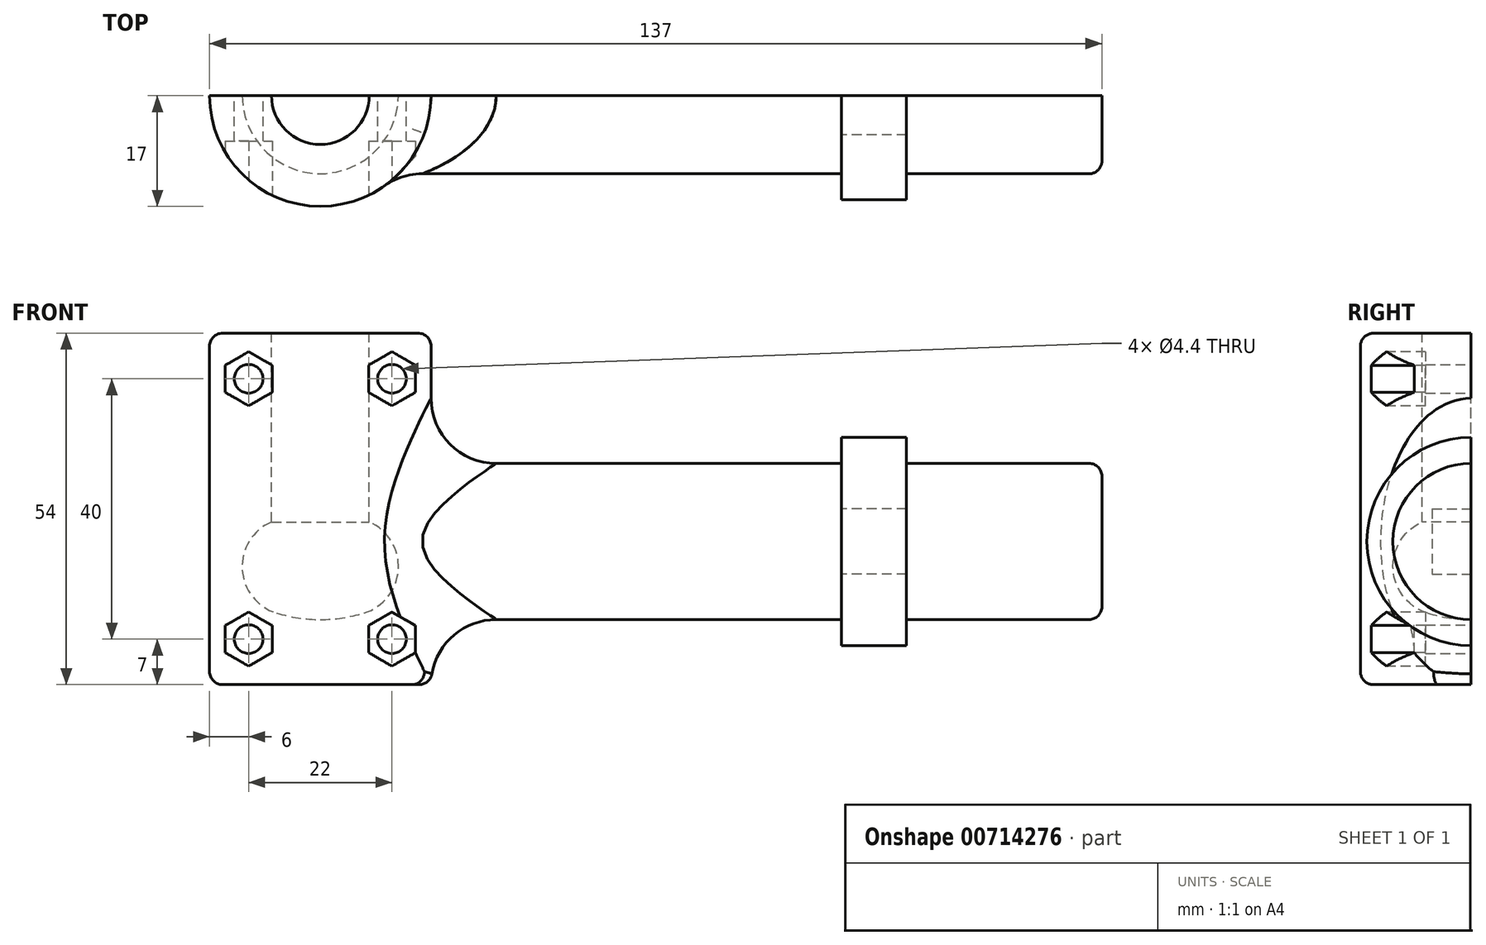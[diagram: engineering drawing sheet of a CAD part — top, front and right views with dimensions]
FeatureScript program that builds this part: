
annotation { "Feature Type Name" : "Feature", "Feature Type Description" : "" }
export const myFeature = defineFeature(function(context is Context, id is Id, definition is map)
    precondition{}
    {
        {
            var Q0;
            Q0=qCreatedBy(makeId("Front.planeOp"),FACE);
            var sketch = newSketch(context, id + "F0", { "sketchPlane" : qUnion([Q0])});
            skLineSegment(sketch, "E0", {"start": v(0, 0) * mm, "end": v(120, 0) * mm});
            skLineSegment(sketch, "E1", {"start": v(0, 0) * mm, "end": v(0, 12) * mm});
            skLineSegment(sketch, "E2", {"start": v(0, 12) * mm, "end": v(80, 12) * mm});
            skLineSegment(sketch, "E3", {"start": v(80, 12) * mm, "end": v(80, 16) * mm});
            skLineSegment(sketch, "E4", {"start": v(80, 16) * mm, "end": v(90, 16) * mm});
            skLineSegment(sketch, "E5", {"start": v(90, 16) * mm, "end": v(90, 12) * mm});
            skLineSegment(sketch, "E6", {"start": v(90, 12) * mm, "end": v(120, 12) * mm});
            skLineSegment(sketch, "E7", {"start": v(120, 12) * mm, "end": v(120, 0) * mm});
            skSolve(sketch);
        }
        {
            var Q0;
            Q0=makeQuery(id+"F0.imprint","IMPRINT",FACE,{"disambiguationData":[TD([[makeQuery(id+"F0.imprint","IMPRINT",EDGE,{"derivedFrom":sQuery(id+"F0.wireOp",EDGE,"E0")}),1.0]])]});
            var Q1;
            Q1=sQuery(id+"F0.wireOp",EDGE,"E0");
            revolve(context, id + "F1", {"surfaceOperationType" : NewSurfaceOperationType.NEW, "entities" : qUnion([Q0]), "axis" : qUnion([Q1]), "revolveType" : RevolveType.ONE_DIRECTION, "angle" : 180 * degree});
        }
        {
            var Q0;
            Q0=qCreatedBy(makeId("Front.planeOp"),FACE);
            var sketch = newSketch(context, id + "F2", { "sketchPlane" : qUnion([Q0])});
            skLineSegment(sketch, "E8", {"start": v(0, -22) * mm, "end": v(0, 32) * mm});
            skLineSegment(sketch, "E9", {"start": v(0, 32) * mm, "end": v(17, 32) * mm});
            skLineSegment(sketch, "E10", {"start": v(17, 32) * mm, "end": v(17, -22) * mm});
            skLineSegment(sketch, "E11", {"start": v(17, -22) * mm, "end": v(0, -22) * mm});
            skSolve(sketch);
        }
        {
            var Q0;
            Q0=makeQuery(id+"F2.imprint","IMPRINT",FACE,{"disambiguationData":[TD([[makeQuery(id+"F2.imprint","IMPRINT",EDGE,{"derivedFrom":sQuery(id+"F2.wireOp",EDGE,"E8")}),-1.0]])]});
            var Q1;
            Q1=sQuery(id+"F2.wireOp",EDGE,"E8");
            revolve(context, id + "F3", {"operationType" : NewBodyOperationType.ADD, "surfaceOperationType" : NewSurfaceOperationType.NEW, "entities" : qUnion([Q0]), "axis" : qUnion([Q1]), "revolveType" : RevolveType.ONE_DIRECTION, "oppositeDirection" : true, "angle" : 180 * degree});
        }
        {
            var Q0;
            Q0=qCreatedBy(makeId("Front.planeOp"),FACE);
            var sketch = newSketch(context, id + "F4", { "sketchPlane" : qUnion([Q0])});
            skLineSegment(sketch, "E12.0", {"start": v(17, 32) * mm, "end": v(-17, 32) * mm});
            skLineSegment(sketch, "E13", {"start": v(0, 0) * mm, "end": v(0, 32) * mm});
            skLineSegment(sketch, "E14", {"start": v(0, 32) * mm, "end": v(7.5, 32) * mm});
            skLineSegment(sketch, "E15", {"start": v(7.5, 32) * mm, "end": v(7.5, 3) * mm});
            skArc(sketch, "E16", {"start": v(6.7, -11) * mm, "mid": v(11.99, -4.28) * mm, "end": v(7.5, 3) * mm});
            skLineSegment(sketch, "E17", {"start": v(0, 0) * mm, "end": v(0, -12) * mm});
            skArc(sketch, "E18", {"start": v(0, -12) * mm, "mid": v(3.4, -11.75) * mm, "end": v(6.7, -11) * mm});
            skLineSegment(sketch, "E19", {"start": v(7.5, 3) * mm, "end": v(0, 3) * mm, "construction": true});
            skPoint(sketch, "E19.endSnap0", {"position": v(0, -6) * mm});
            skSolve(sketch);
        }
        {
            var Q0;
            Q0=makeQuery(id+"F4.imprint","IMPRINT",FACE,{"disambiguationData":[TD([[makeQuery(id+"F4.imprint","IMPRINT",EDGE,{"derivedFrom":sQuery(id+"F4.wireOp",EDGE,"E13")}),-1.0]])]});
            var Q1;
            Q1=sQuery(id+"F4.wireOp",EDGE,"E13");
            revolve(context, id + "F5", {"operationType" : NewBodyOperationType.REMOVE, "surfaceOperationType" : NewSurfaceOperationType.NEW, "entities" : qUnion([Q0]), "axis" : qUnion([Q1]), "revolveType" : RevolveType.FULL, "oppositeDirection" : true});
        }
        {
            var Q0;
            Q0=qCreatedBy(makeId("Front.planeOp"),FACE);
            var sketch = newSketch(context, id + "F6", { "sketchPlane" : qUnion([Q0])});
            skLineSegment(sketch, "E20", {"start": v(11, 25) * mm, "end": v(-11, 25) * mm, "construction": true});
            skLineSegment(sketch, "E21", {"start": v(0, -15) * mm, "end": v(0, 25) * mm, "construction": true});
            skLineSegment(sketch, "E22", {"start": v(11, -15) * mm, "end": v(-11, -15) * mm, "construction": true});
            skSolve(sketch);
        }
        {
            var Q0;
            Q0=sQuery(id+"F6.wireOp",VERTEX,"E20.start");
            var Q1;
            Q1=sQuery(id+"F6.wireOp",VERTEX,"E20.end");
            var Q2;
            Q2=sQuery(id+"F6.wireOp",VERTEX,"E22.start");
            var Q3;
            Q3=sQuery(id+"F6.wireOp",VERTEX,"E22.end");
            var Q4;
            Q4=makeQuery(id+"F1.opRevolve","SWEPT_BODY",BODY,{"disambiguationData":[OSD([sQuery(id+"F0.wireOp",EDGE,"E0"),sQuery(id+"F0.wireOp",EDGE,"E1"),sQuery(id+"F0.wireOp",EDGE,"E2"),sQuery(id+"F0.wireOp",EDGE,"E3"),sQuery(id+"F0.wireOp",EDGE,"E4"),sQuery(id+"F0.wireOp",EDGE,"E5"),sQuery(id+"F0.wireOp",EDGE,"E6"),sQuery(id+"F0.wireOp",EDGE,"E7")])]});
            hole(context, id + "F7", {"style" : HoleStyle.SIMPLE, "endStyle" : HoleEndStyle.THROUGH, "oppositeDirection" : true, "holeDiameter" : 4.4 * mm, "majorDiameter" : 5 * mm, "isTappedThrough" : true, "tappedDepth" : 12 * mm, "tapClearance" : 3, "locations" : qUnion([Q0, Q1, Q2, Q3]), "scope" : qUnion([Q4])});
        }
        {
            var Q0;
            Q0=makeQuery(id+"F3.opRevolve","SWEPT_EDGE",EDGE,{"disambiguationData":[OSD([sQuery(id+"F2.wireOp",EDGE,"E9"),sQuery(id+"F2.wireOp",EDGE,"E10")])]});
            cPoint(context, id + "F8", {"entities" : qUnion([Q0]), "parameter" : 0.5});
        }
        {
            var Q0;
            Q0=qCreatedBy(makeId("Front.planeOp"),FACE);
            var Q1;
            Q1 = qCreatedBy(id + "F8" ,VERTEX);
            cPlane(context, id + "F9", {"entities" : qUnion([Q0, Q1]), "cplaneType" : CPlaneType.PLANE_POINT, "offset" : 25 * mm, "width" : 150 * mm, "height" : 150 * mm});
        }
        {
            var Q0;
            Q0=qCreatedBy(id+"F9.planeOp",FACE);
            var sketch = newSketch(context, id + "F10", { "sketchPlane" : qUnion([Q0])});
            skCircle(sketch, "E23.0", {"center": v(11, -15) * mm, "radius": 2.2 * mm});
            skCircle(sketch, "E24.0", {"center": v(-11, -15) * mm, "radius": 2.2 * mm});
            skCircle(sketch, "E25.0", {"center": v(-11, 25) * mm, "radius": 2.2 * mm});
            skCircle(sketch, "E26.0", {"center": v(11, 25) * mm, "radius": 2.2 * mm});
            skCircle(sketch, "E27.cCircle", {"center": v(-11, 25) * mm, "radius": 3.6 * mm, "construction": true});
            skLineSegment(sketch, "E27.0", {"start": v(-7.4, 27.08) * mm, "end": v(-7.4, 22.92) * mm});
            skLineSegment(sketch, "E27.1", {"start": v(-7.4, 22.92) * mm, "end": v(-11, 20.84) * mm});
            skLineSegment(sketch, "E27.2", {"start": v(-11, 20.84) * mm, "end": v(-14.6, 22.92) * mm});
            skLineSegment(sketch, "E27.3", {"start": v(-14.6, 22.92) * mm, "end": v(-14.6, 27.08) * mm});
            skLineSegment(sketch, "E27.4", {"start": v(-14.6, 27.08) * mm, "end": v(-11, 29.16) * mm});
            skLineSegment(sketch, "E27.5", {"start": v(-11, 29.16) * mm, "end": v(-7.4, 27.08) * mm});
            skPoint(sketch, "E27.0.midPoint", {"position": v(-7.4, 25) * mm});
            skCircle(sketch, "E28.cCircle", {"center": v(11, 25) * mm, "radius": 3.6 * mm, "construction": true});
            skLineSegment(sketch, "E28.0", {"start": v(14.6, 27.08) * mm, "end": v(14.6, 22.92) * mm});
            skLineSegment(sketch, "E28.1", {"start": v(14.6, 22.92) * mm, "end": v(11, 20.84) * mm});
            skLineSegment(sketch, "E28.2", {"start": v(11, 20.84) * mm, "end": v(7.4, 22.92) * mm});
            skLineSegment(sketch, "E28.3", {"start": v(7.4, 22.92) * mm, "end": v(7.4, 27.08) * mm});
            skLineSegment(sketch, "E28.4", {"start": v(7.4, 27.08) * mm, "end": v(11, 29.16) * mm});
            skLineSegment(sketch, "E28.5", {"start": v(11, 29.16) * mm, "end": v(14.6, 27.08) * mm});
            skPoint(sketch, "E28.0.midPoint", {"position": v(14.6, 25) * mm});
            skCircle(sketch, "E29.cCircle", {"center": v(-11, -15) * mm, "radius": 3.6 * mm, "construction": true});
            skLineSegment(sketch, "E29.0", {"start": v(-7.4, -12.92) * mm, "end": v(-7.4, -17.08) * mm});
            skLineSegment(sketch, "E29.1", {"start": v(-7.4, -17.08) * mm, "end": v(-11, -19.16) * mm});
            skLineSegment(sketch, "E29.2", {"start": v(-11, -19.16) * mm, "end": v(-14.6, -17.08) * mm});
            skLineSegment(sketch, "E29.3", {"start": v(-14.6, -17.08) * mm, "end": v(-14.6, -12.92) * mm});
            skLineSegment(sketch, "E29.4", {"start": v(-14.6, -12.92) * mm, "end": v(-11, -10.84) * mm});
            skLineSegment(sketch, "E29.5", {"start": v(-11, -10.84) * mm, "end": v(-7.4, -12.92) * mm});
            skPoint(sketch, "E29.0.midPoint", {"position": v(-7.4, -15) * mm});
            skCircle(sketch, "E30.cCircle", {"center": v(11, -15) * mm, "radius": 3.6 * mm, "construction": true});
            skLineSegment(sketch, "E30.0", {"start": v(14.6, -12.92) * mm, "end": v(14.6, -17.08) * mm});
            skLineSegment(sketch, "E30.1", {"start": v(14.6, -17.08) * mm, "end": v(11, -19.16) * mm});
            skLineSegment(sketch, "E30.2", {"start": v(11, -19.16) * mm, "end": v(7.4, -17.08) * mm});
            skLineSegment(sketch, "E30.3", {"start": v(7.4, -17.08) * mm, "end": v(7.4, -12.92) * mm});
            skLineSegment(sketch, "E30.4", {"start": v(7.4, -12.92) * mm, "end": v(11, -10.84) * mm});
            skLineSegment(sketch, "E30.5", {"start": v(11, -10.84) * mm, "end": v(14.6, -12.92) * mm});
            skPoint(sketch, "E30.0.midPoint", {"position": v(14.6, -15) * mm});
            skSolve(sketch);
        }
        {
            var Q0;
            Q0=makeQuery(id+"F10.imprint","IMPRINT",FACE,{"disambiguationData":[TD([[makeQuery(id+"F10.imprint","IMPRINT",EDGE,{"derivedFrom":sQuery(id+"F10.wireOp",EDGE,"E26.0")}),-1.0]])]});
            var Q1;
            Q1=makeQuery(id+"F10.imprint","IMPRINT",FACE,{"disambiguationData":[TD([[makeQuery(id+"F10.imprint","IMPRINT",EDGE,{"derivedFrom":sQuery(id+"F10.wireOp",EDGE,"E25.0")}),-1.0]])]});
            var Q2;
            Q2=makeQuery(id+"F10.imprint","IMPRINT",FACE,{"disambiguationData":[TD([[makeQuery(id+"F10.imprint","IMPRINT",EDGE,{"derivedFrom":sQuery(id+"F10.wireOp",EDGE,"E24.0")}),-1.0]])]});
            var Q3;
            Q3=makeQuery(id+"F10.imprint","IMPRINT",FACE,{"disambiguationData":[TD([[makeQuery(id+"F10.imprint","IMPRINT",EDGE,{"derivedFrom":sQuery(id+"F10.wireOp",EDGE,"E23.0")}),-1.0]])]});
            extrude(context, id + "F11", {"entities" : qUnion([Q0, Q1, Q2, Q3]), "operationType" : NewBodyOperationType.REMOVE, "oppositeDirection" : true, "depth" : 10 * mm, "offsetDistance" : 25 * mm});
        }
        {
            var Q0;
            Q0=makeQuery(id+"F3.boolean.opBoolean","INTERSECT",EDGE,{"derivedFrom":[makeQuery(id+"F1.opRevolve","SWEPT_FACE",FACE,{"disambiguationData":[OSD([sQuery(id+"F0.wireOp",EDGE,"E2")])]}),makeQuery(id+"F3.opRevolve","SWEPT_FACE",FACE,{"disambiguationData":[OSD([sQuery(id+"F2.wireOp",EDGE,"E10")])]})]});
            fillet(context, id + "F12", {"entities" : qUnion([Q0]), "radius" : 10 * mm, "tangentPropagation" : true, "allowEdgeOverflow" : false});
        }
        {
            var Q0;
            Q0=makeQuery(id+"F3.opRevolve","SWEPT_EDGE",EDGE,{"disambiguationData":[OSD([sQuery(id+"F2.wireOp",EDGE,"E10"),sQuery(id+"F2.wireOp",EDGE,"E11")])]});
            var Q1;
            Q1=makeQuery(id+"F3.opRevolve","SWEPT_EDGE",EDGE,{"disambiguationData":[OSD([sQuery(id+"F2.wireOp",EDGE,"E9"),sQuery(id+"F2.wireOp",EDGE,"E10")])]});
            var Q2;
            Q2=makeQuery(id+"F1.opRevolve","SWEPT_EDGE",EDGE,{"disambiguationData":[OSD([sQuery(id+"F0.wireOp",EDGE,"E6"),sQuery(id+"F0.wireOp",EDGE,"E7")])]});
            fillet(context, id + "F13", {"entities" : qUnion([Q0, Q1, Q2]), "radius" : 2 * mm, "tangentPropagation" : true, "allowEdgeOverflow" : false});
        }
        {
            var Q0;
            Q0=makeQuery(id+"F3.boolean.opBoolean","MERGE",FACE,{"derivedFrom":[makeQuery(id+"F1.opRevolve","CAP_FACE",FACE,{"disambiguationData":[OSD([sQuery(id+"F0.wireOp",EDGE,"E0"),sQuery(id+"F0.wireOp",EDGE,"E1"),sQuery(id+"F0.wireOp",EDGE,"E2"),sQuery(id+"F0.wireOp",EDGE,"E3"),sQuery(id+"F0.wireOp",EDGE,"E4"),sQuery(id+"F0.wireOp",EDGE,"E5"),sQuery(id+"F0.wireOp",EDGE,"E6"),sQuery(id+"F0.wireOp",EDGE,"E7")])],"isStart":true}),makeQuery(id+"F3.opRevolve","CAP_FACE",FACE,{"disambiguationData":[OSD([sQuery(id+"F2.wireOp",EDGE,"E8"),sQuery(id+"F2.wireOp",EDGE,"E9"),sQuery(id+"F2.wireOp",EDGE,"E10"),sQuery(id+"F2.wireOp",EDGE,"E11")])],"isStart":false})]});
            var sketch = newSketch(context, id + "F14", { "sketchPlane" : qUnion([Q0])});
            skLineSegment(sketch, "E31.bottom", {"start": v(-90, 5) * mm, "end": v(-80, 5) * mm});
            skLineSegment(sketch, "E31.top", {"start": v(-90, -5) * mm, "end": v(-80, -5) * mm});
            skLineSegment(sketch, "E31.left", {"start": v(-90, 5) * mm, "end": v(-90, -5) * mm});
            skLineSegment(sketch, "E31.right", {"start": v(-80, 5) * mm, "end": v(-80, -5) * mm});
            skPoint(sketch, "E32.0", {"position": v(-120, 0) * mm});
            skLineSegment(sketch, "E33", {"start": v(-90, 0) * mm, "end": v(-80, 0) * mm, "construction": true});
            skSolve(sketch);
        }
        {
            var Q0;
            Q0=makeQuery(id+"F14.imprint","IMPRINT",FACE,{"disambiguationData":[TD([[makeQuery(id+"F14.imprint","IMPRINT",EDGE,{"derivedFrom":sQuery(id+"F14.wireOp",EDGE,"E31.bottom")}),-1.0]])]});
            extrude(context, id + "F15", {"entities" : qUnion([Q0]), "operationType" : NewBodyOperationType.REMOVE, "oppositeDirection" : true, "depth" : 6 * mm, "offsetDistance" : 25 * mm});
        }
    });
